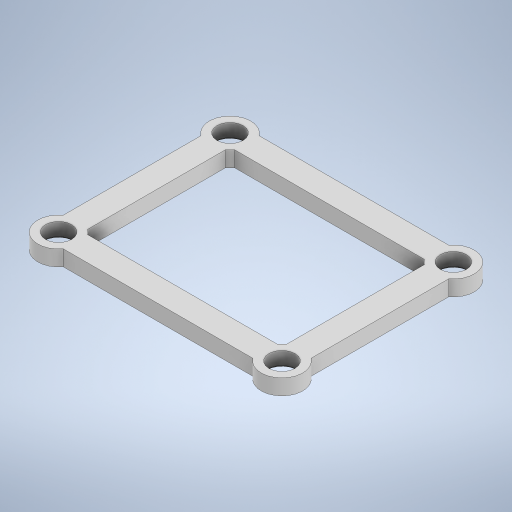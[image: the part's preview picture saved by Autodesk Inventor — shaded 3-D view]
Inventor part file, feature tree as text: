
AUTODESK INVENTOR PART (.ipt)
format: ipt  version: 2024.2 (Build 282272000, 272)  size: 292,352 bytes
history: native  units: mm
features: extrude x1, chamfer x1, sketch x1
ambient origin geometry x8: Origin, YZ Plane, XZ Plane, XY Plane, X Axis, Y Axis, Z Axis, Center Point
bodies: Solid1 (feature_tree)
feature tree (3):
  extrude  "Extrusion1"  Depth=3.0mm
  chamfer  "Chamfer1"  Distance=5.0mm
  sketch  "Sketch1"  dims[d0=5.0mm d1=8.0mm d2=5.0mm d3=8.0mm d4=5.0mm d5=8.0mm d6=5.0mm d7=8.0mm d8=4.0mm d9=4.0mm d10=4.0mm d11=4.0mm d12=4.0mm d13=4.0mm d14=4.0mm d15=4.0mm d16=33.0mm d17=4.7mm d18=4.7mm d19=4.7mm d20=4.7mm d21=2.35mm d22=2.35mm d23=2.35mm d24=2.35mm d25=43.0mm d26=3.0mm d27=0.0mm d28=0.5mm d29=2.0mm d30=45.0deg]
